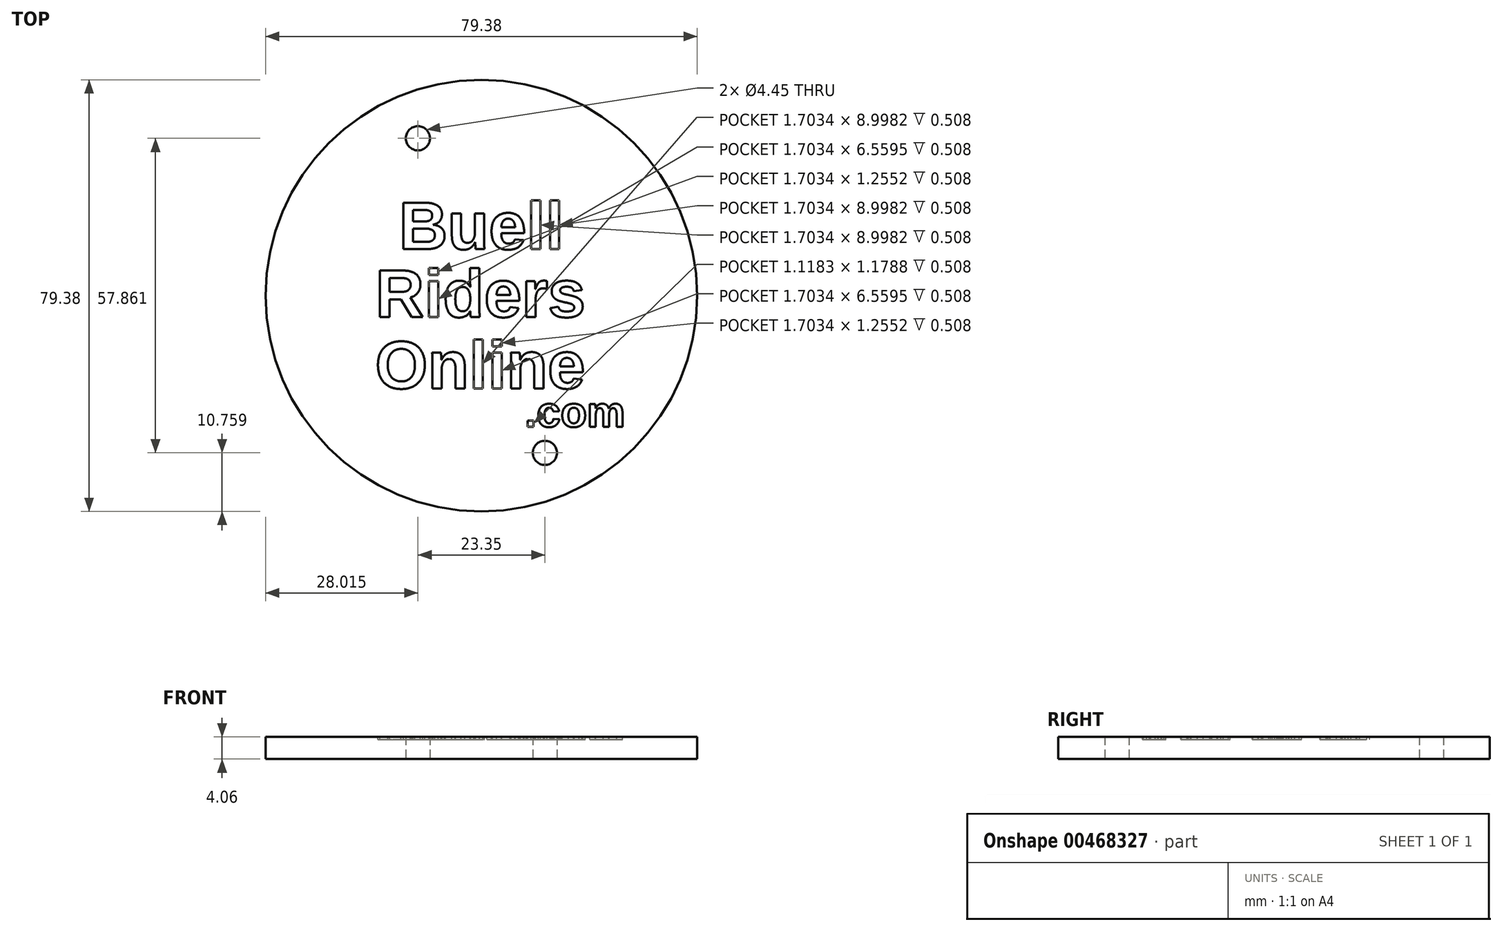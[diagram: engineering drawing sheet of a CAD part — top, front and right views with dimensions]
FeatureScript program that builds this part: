
annotation { "Feature Type Name" : "Feature", "Feature Type Description" : "" }
export const myFeature = defineFeature(function(context is Context, id is Id, definition is map)
    precondition{}
    {
        {
            var Q0;
            Q0=qCreatedBy(makeId("Top.planeOp"),FACE);
            var sketch = newSketch(context, id + "F0", { "sketchPlane" : qUnion([Q0])});
            skCircle(sketch, "E0", {"center": v(0, 0) * mm, "radius": 39.69 * mm});
            skCircle(sketch, "E1", {"center": v(-11.67, 28.93) * mm, "radius": 2.22 * mm});
            skCircle(sketch, "E2", {"center": v(11.67, -28.93) * mm, "radius": 2.22 * mm});
            skPoint(sketch, "E3", {"position": v(0, 39.69) * mm});
            skSolve(sketch);
        }
        {
            var Q0;
            Q0=makeQuery(id+"F0.imprint","IMPRINT",FACE,{"disambiguationData":[TD([[makeQuery(id+"F0.imprint","IMPRINT",EDGE,{"derivedFrom":sQuery(id+"F0.wireOp",EDGE,"E0")}),1.0]])]});
            extrude(context, id + "F1", {"entities" : qUnion([Q0]), "depth" : 4.06 * mm});
        }
        {
            var Q0;
            Q0=makeQuery(id+"F1.opExtrude","CAP_FACE",FACE,{"disambiguationData":[OSD([sQuery(id+"F0.wireOp",EDGE,"E0"),sQuery(id+"F0.wireOp",EDGE,"E1"),sQuery(id+"F0.wireOp",EDGE,"E2")])],"isStart":false});
            var sketch = newSketch(context, id + "F2", { "sketchPlane" : qUnion([Q0])});
            skText(sketch, "E4", { "text": "Buell", "fontName": "Arimo-Bold.ttf"});
            skText(sketch, "E5", { "text": "Riders", "fontName": "Arimo-Bold.ttf"});
            skText(sketch, "E6", { "text": "Online", "fontName": "Arimo-Bold.ttf"});
            skText(sketch, "E7", { "text": ".com", "fontName": "Arimo-Bold.ttf"});
            const initialGuessF2  = {"E4": [-0.01517, 0.00854, 1, 0, 0.00894], "E5": [-0.0195, -0.00393, 1, 0, 0.00894], "E6": [-0.01954, -0.01707, 1, 0, 0.00894], "E7": [0.00796, -0.02415, 1, 0, 0.0057]};
            skSetInitialGuess(sketch, initialGuessF2);
            skSolve(sketch);
        }
        {
            var Q0;
            Q0=qSketchRegion(id+"F2",true);
            extrude(context, id + "F3", {"entities" : qUnion([Q0]), "operationType" : NewBodyOperationType.REMOVE, "oppositeDirection" : true, "depth" : 0.5 * mm});
        }
    });
